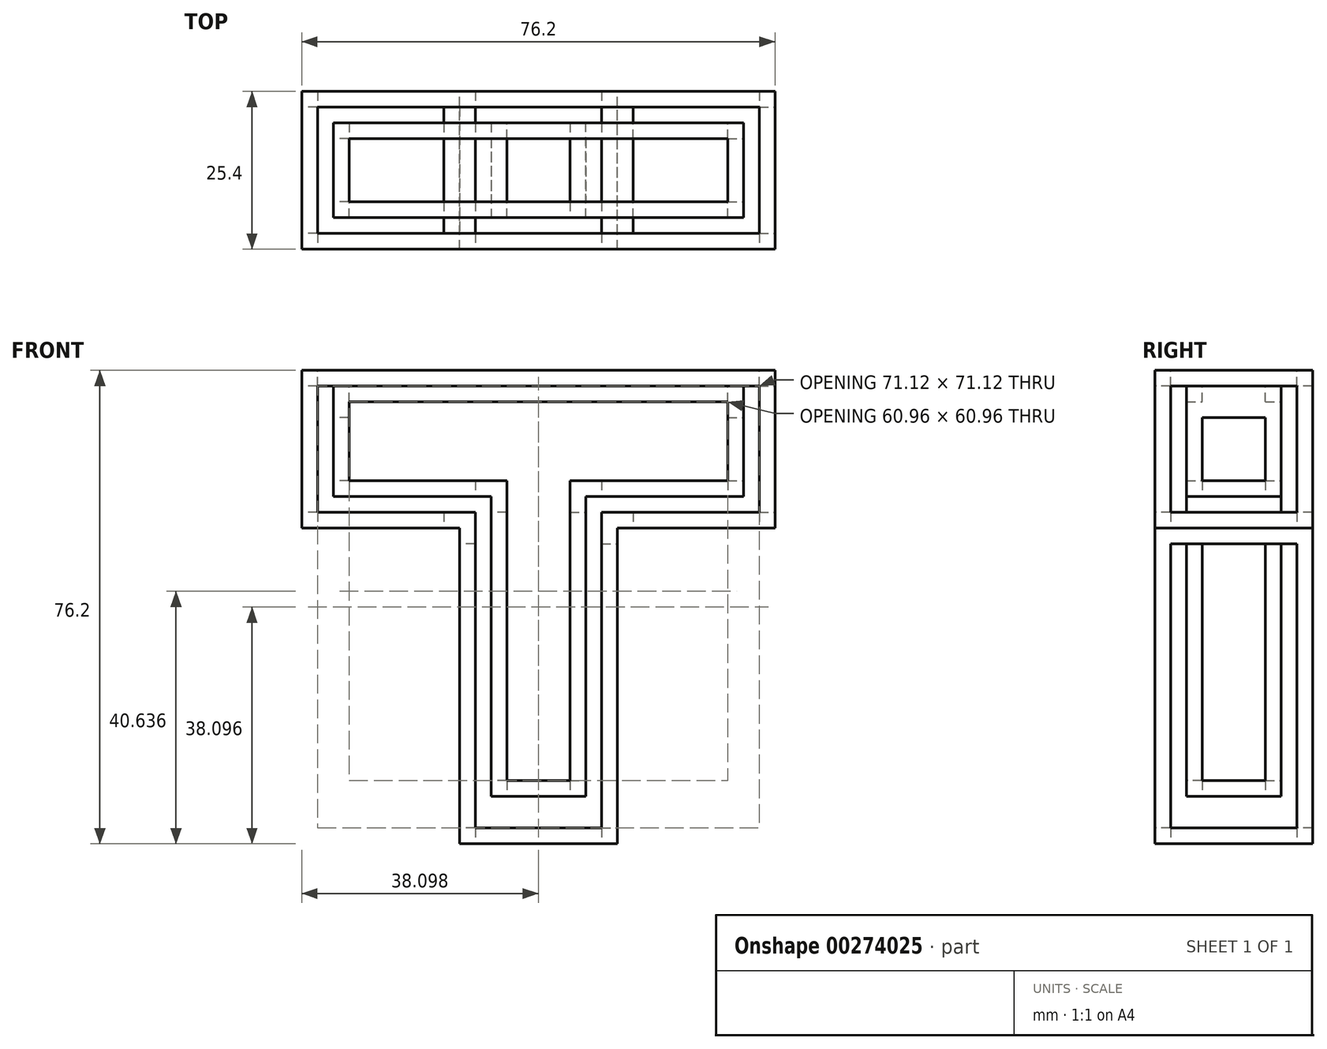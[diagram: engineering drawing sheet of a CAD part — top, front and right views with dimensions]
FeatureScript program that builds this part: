
annotation { "Feature Type Name" : "Feature", "Feature Type Description" : "" }
export const myFeature = defineFeature(function(context is Context, id is Id, definition is map)
    precondition{}
    {
        {
            var Q0;
            Q0=qCreatedBy(makeId("Front.planeOp"),FACE);
            var sketch = newSketch(context, id + "F0", { "sketchPlane" : qUnion([Q0])});
            skCircle(sketch, "E0.cCircle", {"center": v(-31.95, 20.43) * mm, "radius": 23.31 * mm, "construction": true});
            skLineSegment(sketch, "E0.0", {"start": v(-8.63, 33.9) * mm, "end": v(-8.63, 6.97) * mm});
            skLineSegment(sketch, "E0.1", {"start": v(-8.63, 6.97) * mm, "end": v(-31.95, -6.48) * mm});
            skLineSegment(sketch, "E0.2", {"start": v(-31.95, -6.48) * mm, "end": v(-55.26, 6.97) * mm});
            skLineSegment(sketch, "E0.3", {"start": v(-55.26, 6.97) * mm, "end": v(-55.26, 33.9) * mm});
            skLineSegment(sketch, "E0.4", {"start": v(-55.26, 33.9) * mm, "end": v(-31.95, 47.35) * mm});
            skLineSegment(sketch, "E0.5", {"start": v(-31.95, 47.35) * mm, "end": v(-8.63, 33.9) * mm});
            skPoint(sketch, "E0.0.midPoint", {"position": v(-8.63, 20.43) * mm});
            skSolve(sketch);
        }
        {
            var Q0;
            Q0 = qSketchRegion(id + "F0", true);
            extrude(context, id + "F1", {"entities" : qUnion([Q0]), "depth" : 25.4 * mm});
        }
        {
            var Q0;
            Q0=makeQuery(id+"F1.opExtrude","SWEPT_BODY",BODY,{"disambiguationData":[OSD([sQuery(id+"F0.wireOp",EDGE,"E0.0"),sQuery(id+"F0.wireOp",EDGE,"E0.1"),sQuery(id+"F0.wireOp",EDGE,"E0.2"),sQuery(id+"F0.wireOp",EDGE,"E0.3"),sQuery(id+"F0.wireOp",EDGE,"E0.4"),sQuery(id+"F0.wireOp",EDGE,"E0.5")])]});
            deleteBodies(context, id + "F2", {"entities" : qUnion([Q0])});
        }
        {
            var Q0;
            Q0=qCreatedBy(makeId("Front.planeOp"),FACE);
            var sketch = newSketch(context, id + "F3", { "sketchPlane" : qUnion([Q0])});
            skLineSegment(sketch, "E1", {"start": v(-61.41, 28.32) * mm, "end": v(14.79, 28.32) * mm});
            skLineSegment(sketch, "E2", {"start": v(14.79, 28.32) * mm, "end": v(14.79, 2.92) * mm});
            skLineSegment(sketch, "E3", {"start": v(14.79, 2.92) * mm, "end": v(-61.41, 2.92) * mm});
            skLineSegment(sketch, "E4", {"start": v(-61.41, 2.92) * mm, "end": v(-61.41, 28.32) * mm});
            skLineSegment(sketch, "E5", {"start": v(-23.31, 2.92) * mm, "end": v(-23.31, -47.88) * mm});
            skLineSegment(sketch, "E6", {"start": v(-23.31, -47.88) * mm, "end": v(-36.01, -47.88) * mm});
            skLineSegment(sketch, "E7", {"start": v(-36.01, -47.88) * mm, "end": v(-36.01, 2.92) * mm});
            skLineSegment(sketch, "E8", {"start": v(-23.31, -47.88) * mm, "end": v(-10.61, -47.88) * mm});
            skLineSegment(sketch, "E9", {"start": v(-10.61, -47.88) * mm, "end": v(-10.61, 2.92) * mm});
            skSolve(sketch);
        }
        {
            var Q0;
            Q0=makeQuery(id+"F3.imprint","IMPRINT",FACE,{"disambiguationData":[TD([[makeQuery(id+"F3.imprint","IMPRINT",EDGE,{"derivedFrom":sQuery(id+"F3.wireOp",EDGE,"E1")}),-1.0]])]});
            var Q1;
            {var subQ0=sQuery(id+"F3.wireOp",EDGE,"E5");Q1=makeQuery(id+"F3.imprint","IMPRINT",FACE,{"disambiguationData":[TD([[makeQuery(id+"F3.imprint","IMPRINT",EDGE,{"derivedFrom":subQ0}),-1.0]])]});}
            var Q2;
            {var subQ0=sQuery(id+"F3.wireOp",EDGE,"E5");Q2=makeQuery(id+"F3.imprint","IMPRINT",FACE,{"disambiguationData":[TD([[makeQuery(id+"F3.imprint","IMPRINT",EDGE,{"derivedFrom":subQ0}),1.0]])]});}
            extrude(context, id + "F4", {"entities" : qUnion([Q0, Q1, Q2]), "depth" : 12.7 * mm});
        }
        {
            var Q0;
            Q0=makeQuery(id+"F4.opExtrude","CAP_FACE",FACE,{"disambiguationData":[OSD([sQuery(id+"F3.wireOp",EDGE,"E1"),sQuery(id+"F3.wireOp",EDGE,"E2"),sQuery(id+"F3.wireOp",EDGE,"E3"),sQuery(id+"F3.wireOp",EDGE,"E4"),sQuery(id+"F3.wireOp",EDGE,"E6"),sQuery(id+"F3.wireOp",EDGE,"E7"),sQuery(id+"F3.wireOp",EDGE,"E8"),sQuery(id+"F3.wireOp",EDGE,"E9")])],"isStart":false});
            var sketch = newSketch(context, id + "F5", { "sketchPlane" : qUnion([Q0])});
            skLineSegment(sketch, "E10.0", {"start": v(-33.47, -45.34) * mm, "end": v(-13.15, -45.34) * mm});
            skLineSegment(sketch, "E10.1", {"start": v(-33.47, 5.46) * mm, "end": v(-33.47, -45.34) * mm});
            skLineSegment(sketch, "E10.2", {"start": v(-13.15, -45.34) * mm, "end": v(-13.15, 5.46) * mm});
            skLineSegment(sketch, "E10.3", {"start": v(-58.87, 5.46) * mm, "end": v(-33.47, 5.46) * mm});
            skLineSegment(sketch, "E10.4", {"start": v(-13.15, 5.46) * mm, "end": v(12.25, 5.46) * mm});
            skLineSegment(sketch, "E10.5", {"start": v(12.25, 5.46) * mm, "end": v(12.25, 25.78) * mm});
            skLineSegment(sketch, "E10.6", {"start": v(12.25, 25.78) * mm, "end": v(-58.87, 25.78) * mm});
            skLineSegment(sketch, "E10.7", {"start": v(-58.87, 25.78) * mm, "end": v(-58.87, 5.46) * mm});
            skSolve(sketch);
        }
        {
            var Q0;
            Q0=makeQuery(id+"F5.imprint","IMPRINT",FACE,{"disambiguationData":[TD([[makeQuery(id+"F5.imprint","IMPRINT",EDGE,{"derivedFrom":sQuery(id+"F5.wireOp",EDGE,"E10.0")}),1.0]])]});
            extrude(context, id + "F6", {"entities" : qUnion([Q0]), "operationType" : NewBodyOperationType.REMOVE, "oppositeDirection" : true, "depth" : 5.08 * mm});
        }
        {
            var Q0;
            Q0=makeQuery(id+"F4.opExtrude","SWEPT_BODY",BODY,{"disambiguationData":[OSD([sQuery(id+"F3.wireOp",EDGE,"E1"),sQuery(id+"F3.wireOp",EDGE,"E2"),sQuery(id+"F3.wireOp",EDGE,"E3"),sQuery(id+"F3.wireOp",EDGE,"E4"),sQuery(id+"F3.wireOp",EDGE,"E6"),sQuery(id+"F3.wireOp",EDGE,"E7"),sQuery(id+"F3.wireOp",EDGE,"E8"),sQuery(id+"F3.wireOp",EDGE,"E9")])]});
            var Q1;
            Q1=makeQuery(id+"F4.opExtrude","CAP_FACE",FACE,{"disambiguationData":[OSD([sQuery(id+"F3.wireOp",EDGE,"E1"),sQuery(id+"F3.wireOp",EDGE,"E2"),sQuery(id+"F3.wireOp",EDGE,"E3"),sQuery(id+"F3.wireOp",EDGE,"E4"),sQuery(id+"F3.wireOp",EDGE,"E6"),sQuery(id+"F3.wireOp",EDGE,"E7"),sQuery(id+"F3.wireOp",EDGE,"E8"),sQuery(id+"F3.wireOp",EDGE,"E9")])],"isStart":true});
            mirror(context, id + "F7", {"operationType" : NewBodyOperationType.ADD, "entities" : qUnion([Q0]), "mirrorPlane" : qUnion([Q1])});
        }
        {
            var Q0;
            Q0=makeQuery(id+"F7.opPattern","COPY",FACE,{"derivedFrom":makeQuery(id+"F6.boolean.opBoolean","COPY",FACE,{"derivedFrom":makeQuery(id+"F6.opExtrude","CAP_FACE",FACE,{"disambiguationData":[OSD([sQuery(id+"F5.wireOp",EDGE,"E10.0"),sQuery(id+"F5.wireOp",EDGE,"E10.1"),sQuery(id+"F5.wireOp",EDGE,"E10.2"),sQuery(id+"F5.wireOp",EDGE,"E10.3"),sQuery(id+"F5.wireOp",EDGE,"E10.4"),sQuery(id+"F5.wireOp",EDGE,"E10.5"),sQuery(id+"F5.wireOp",EDGE,"E10.6"),sQuery(id+"F5.wireOp",EDGE,"E10.7")])],"isStart":false})}),"instanceName":"1"});
            var sketch = newSketch(context, id + "F8", { "sketchPlane" : qUnion([Q0])});
            skLineSegment(sketch, "E11.0", {"start": v(56.33, 8) * mm, "end": v(56.33, 23.24) * mm});
            skLineSegment(sketch, "E11.1", {"start": v(30.93, 8) * mm, "end": v(56.33, 8) * mm});
            skLineSegment(sketch, "E11.2", {"start": v(56.33, 23.24) * mm, "end": v(-9.7, 23.24) * mm});
            skLineSegment(sketch, "E11.3", {"start": v(30.93, -42.8) * mm, "end": v(30.93, 8) * mm});
            skLineSegment(sketch, "E11.4", {"start": v(-9.7, 23.24) * mm, "end": v(-9.7, 8) * mm});
            skLineSegment(sketch, "E11.5", {"start": v(-9.7, 8) * mm, "end": v(15.7, 8) * mm});
            skLineSegment(sketch, "E11.6", {"start": v(15.7, 8) * mm, "end": v(15.7, -42.8) * mm});
            skLineSegment(sketch, "E11.7", {"start": v(15.7, -42.8) * mm, "end": v(30.93, -42.8) * mm});
            skSolve(sketch);
        }
        {
            var Q0;
            Q0=makeQuery(id+"F8.imprint","IMPRINT",FACE,{"disambiguationData":[TD([[makeQuery(id+"F8.imprint","IMPRINT",EDGE,{"derivedFrom":sQuery(id+"F8.wireOp",EDGE,"E11.0")}),-1.0]])]});
            extrude(context, id + "F9", {"entities" : qUnion([Q0]), "operationType" : NewBodyOperationType.REMOVE, "oppositeDirection" : true, "depth" : 25.4 * mm});
        }
        {
            var Q0;
            Q0=makeQuery(id+"F7.opPattern","COPY",FACE,{"derivedFrom":makeQuery(id+"F6.boolean.opBoolean","COPY",FACE,{"derivedFrom":makeQuery(id+"F6.opExtrude","CAP_FACE",FACE,{"disambiguationData":[OSD([sQuery(id+"F5.wireOp",EDGE,"E10.0"),sQuery(id+"F5.wireOp",EDGE,"E10.1"),sQuery(id+"F5.wireOp",EDGE,"E10.2"),sQuery(id+"F5.wireOp",EDGE,"E10.3"),sQuery(id+"F5.wireOp",EDGE,"E10.4"),sQuery(id+"F5.wireOp",EDGE,"E10.5"),sQuery(id+"F5.wireOp",EDGE,"E10.6"),sQuery(id+"F5.wireOp",EDGE,"E10.7")])],"isStart":false})}),"instanceName":"1"});
            var sketch = newSketch(context, id + "F10", { "sketchPlane" : qUnion([Q0])});
            skLineSegment(sketch, "E12.0", {"start": v(-7.17, 10.54) * mm, "end": v(18.23, 10.54) * mm});
            skLineSegment(sketch, "E12.1", {"start": v(-7.17, 20.7) * mm, "end": v(-7.17, 10.54) * mm});
            skLineSegment(sketch, "E12.2", {"start": v(18.23, 10.54) * mm, "end": v(18.23, -40.26) * mm});
            skLineSegment(sketch, "E12.3", {"start": v(53.8, 20.7) * mm, "end": v(-7.17, 20.7) * mm});
            skLineSegment(sketch, "E12.4", {"start": v(18.23, -40.26) * mm, "end": v(28.4, -40.26) * mm});
            skLineSegment(sketch, "E12.5", {"start": v(28.4, -40.26) * mm, "end": v(28.4, 10.54) * mm});
            skLineSegment(sketch, "E12.6", {"start": v(28.4, 10.54) * mm, "end": v(53.8, 10.54) * mm});
            skLineSegment(sketch, "E12.7", {"start": v(53.8, 10.54) * mm, "end": v(53.8, 20.7) * mm});
            skSolve(sketch);
        }
        {
            var Q0;
            Q0=makeQuery(id+"F10.imprint","IMPRINT",FACE,{"disambiguationData":[TD([[makeQuery(id+"F10.imprint","IMPRINT",EDGE,{"derivedFrom":sQuery(id+"F10.wireOp",EDGE,"E12.0")}),1.0]])]});
            extrude(context, id + "F11", {"entities" : qUnion([Q0]), "operationType" : NewBodyOperationType.REMOVE, "oppositeDirection" : true, "depth" : 25.4 * mm});
        }
        {
            var Q0;
            {var subQ0=makeQuery(id+"F4.opExtrude","SWEPT_FACE",FACE,{"disambiguationData":[OSD([sQuery(id+"F3.wireOp",EDGE,"E9")])]});Q0=makeQuery(id+"F7.boolean.opBoolean","MERGE",FACE,{"derivedFrom":[subQ0,makeQuery(id+"F7.opPattern","COPY",FACE,{"derivedFrom":subQ0,"instanceName":"1"})]});}
            var sketch = newSketch(context, id + "F12", { "sketchPlane" : qUnion([Q0])});
            skLineSegment(sketch, "E13.0", {"start": v(-10.16, -45.34) * mm, "end": v(10.16, -45.34) * mm});
            skLineSegment(sketch, "E13.1", {"start": v(-10.16, 0.38) * mm, "end": v(-10.16, -45.34) * mm});
            skLineSegment(sketch, "E13.2", {"start": v(10.16, 0.38) * mm, "end": v(-10.16, 0.38) * mm});
            skLineSegment(sketch, "E13.3", {"start": v(10.16, -45.34) * mm, "end": v(10.16, 0.38) * mm});
            skSolve(sketch);
        }
        {
            var Q0;
            Q0=makeQuery(id+"F12.imprint","IMPRINT",FACE,{"disambiguationData":[TD([[makeQuery(id+"F12.imprint","IMPRINT",EDGE,{"derivedFrom":sQuery(id+"F12.wireOp",EDGE,"E13.0")}),1.0]])]});
            extrude(context, id + "F13", {"entities" : qUnion([Q0]), "operationType" : NewBodyOperationType.REMOVE, "oppositeDirection" : true, "depth" : 2.54 * mm});
        }
        {
            var Q0;
            {var subQ0=makeQuery(id+"F4.opExtrude","SWEPT_FACE",FACE,{"disambiguationData":[OSD([sQuery(id+"F3.wireOp",EDGE,"E7")])]});Q0=makeQuery(id+"F7.boolean.opBoolean","MERGE",FACE,{"derivedFrom":[subQ0,makeQuery(id+"F7.opPattern","COPY",FACE,{"derivedFrom":subQ0,"instanceName":"1"})]});}
            var sketch = newSketch(context, id + "F14", { "sketchPlane" : qUnion([Q0])});
            skLineSegment(sketch, "E14.0", {"start": v(10.16, 0.38) * mm, "end": v(-10.16, 0.38) * mm});
            skLineSegment(sketch, "E14.1", {"start": v(10.16, -45.34) * mm, "end": v(10.16, 0.38) * mm});
            skLineSegment(sketch, "E14.2", {"start": v(-10.16, -45.34) * mm, "end": v(10.16, -45.34) * mm});
            skLineSegment(sketch, "E14.3", {"start": v(-10.16, 0.38) * mm, "end": v(-10.16, -45.34) * mm});
            skSolve(sketch);
        }
        {
            var Q0;
            Q0=makeQuery(id+"F14.imprint","IMPRINT",FACE,{"disambiguationData":[TD([[makeQuery(id+"F14.imprint","IMPRINT",EDGE,{"derivedFrom":sQuery(id+"F14.wireOp",EDGE,"E14.0")}),1.0]])]});
            extrude(context, id + "F15", {"entities" : qUnion([Q0]), "operationType" : NewBodyOperationType.REMOVE, "oppositeDirection" : true, "depth" : 2.54 * mm});
        }
        {
            var Q0;
            {var subQ0=makeQuery(id+"F4.opExtrude","SWEPT_FACE",FACE,{"disambiguationData":[OSD([sQuery(id+"F3.wireOp",EDGE,"E2")])]});Q0=makeQuery(id+"F7.boolean.opBoolean","MERGE",FACE,{"derivedFrom":[subQ0,makeQuery(id+"F7.opPattern","COPY",FACE,{"derivedFrom":subQ0,"instanceName":"1"})]});}
            var sketch = newSketch(context, id + "F16", { "sketchPlane" : qUnion([Q0])});
            skLineSegment(sketch, "E15.0", {"start": v(-10.16, 5.46) * mm, "end": v(10.16, 5.46) * mm});
            skLineSegment(sketch, "E15.1", {"start": v(-10.16, 25.78) * mm, "end": v(-10.16, 5.46) * mm});
            skLineSegment(sketch, "E15.2", {"start": v(10.16, 25.78) * mm, "end": v(-10.16, 25.78) * mm});
            skLineSegment(sketch, "E15.3", {"start": v(10.16, 5.46) * mm, "end": v(10.16, 25.78) * mm});
            skSolve(sketch);
        }
        {
            var Q0;
            Q0=makeQuery(id+"F16.imprint","IMPRINT",FACE,{"disambiguationData":[TD([[makeQuery(id+"F16.imprint","IMPRINT",EDGE,{"derivedFrom":sQuery(id+"F16.wireOp",EDGE,"E15.0")}),1.0]])]});
            extrude(context, id + "F17", {"entities" : qUnion([Q0]), "operationType" : NewBodyOperationType.REMOVE, "oppositeDirection" : true, "depth" : 2.54 * mm});
        }
        {
            var Q0;
            {var subQ0=makeQuery(id+"F4.opExtrude","SWEPT_FACE",FACE,{"disambiguationData":[OSD([sQuery(id+"F3.wireOp",EDGE,"E4")])]});Q0=makeQuery(id+"F7.boolean.opBoolean","MERGE",FACE,{"derivedFrom":[subQ0,makeQuery(id+"F7.opPattern","COPY",FACE,{"derivedFrom":subQ0,"instanceName":"1"})]});}
            var sketch = newSketch(context, id + "F18", { "sketchPlane" : qUnion([Q0])});
            skLineSegment(sketch, "E16.0", {"start": v(10.16, 25.78) * mm, "end": v(-10.16, 25.78) * mm});
            skLineSegment(sketch, "E16.1", {"start": v(10.16, 5.46) * mm, "end": v(10.16, 25.78) * mm});
            skLineSegment(sketch, "E16.2", {"start": v(-10.16, 5.46) * mm, "end": v(10.16, 5.46) * mm});
            skLineSegment(sketch, "E16.3", {"start": v(-10.16, 25.78) * mm, "end": v(-10.16, 5.46) * mm});
            skSolve(sketch);
        }
        {
            var Q0;
            Q0=makeQuery(id+"F18.imprint","IMPRINT",FACE,{"disambiguationData":[TD([[makeQuery(id+"F18.imprint","IMPRINT",EDGE,{"derivedFrom":sQuery(id+"F18.wireOp",EDGE,"E16.0")}),1.0]])]});
            extrude(context, id + "F19", {"entities" : qUnion([Q0]), "operationType" : NewBodyOperationType.REMOVE, "oppositeDirection" : true, "depth" : 2.54 * mm});
        }
        {
            var Q0;
            {var subQ0=makeQuery(id+"F4.opExtrude","SWEPT_FACE",FACE,{"disambiguationData":[OSD([sQuery(id+"F3.wireOp",EDGE,"E6"),sQuery(id+"F3.wireOp",EDGE,"E8")])]});Q0=makeQuery(id+"F7.boolean.opBoolean","MERGE",FACE,{"derivedFrom":[subQ0,makeQuery(id+"F7.opPattern","COPY",FACE,{"derivedFrom":subQ0,"instanceName":"1"})]});}
            var sketch = newSketch(context, id + "F20", { "sketchPlane" : qUnion([Q0])});
            skLineSegment(sketch, "E17.0", {"start": v(-33.47, 10.16) * mm, "end": v(-33.47, -10.16) * mm});
            skLineSegment(sketch, "E17.1", {"start": v(-13.15, 10.16) * mm, "end": v(-33.47, 10.16) * mm});
            skLineSegment(sketch, "E17.2", {"start": v(-13.15, -10.16) * mm, "end": v(-13.15, 10.16) * mm});
            skLineSegment(sketch, "E17.3", {"start": v(-33.47, -10.16) * mm, "end": v(-13.15, -10.16) * mm});
            skSolve(sketch);
        }
        {
            var Q0;
            Q0=makeQuery(id+"F20.imprint","IMPRINT",FACE,{"disambiguationData":[TD([[makeQuery(id+"F20.imprint","IMPRINT",EDGE,{"derivedFrom":sQuery(id+"F20.wireOp",EDGE,"E17.0")}),1.0]])]});
            extrude(context, id + "F21", {"entities" : qUnion([Q0]), "operationType" : NewBodyOperationType.REMOVE, "oppositeDirection" : true, "depth" : 2.54 * mm});
        }
        {
            var Q0;
            {var subQ0=makeQuery(id+"F4.opExtrude","SWEPT_FACE",FACE,{"disambiguationData":[OSD([sQuery(id+"F3.wireOp",EDGE,"E1")])]});Q0=makeQuery(id+"F7.boolean.opBoolean","MERGE",FACE,{"derivedFrom":[subQ0,makeQuery(id+"F7.opPattern","COPY",FACE,{"derivedFrom":subQ0,"instanceName":"1"})]});}
            var sketch = newSketch(context, id + "F22", { "sketchPlane" : qUnion([Q0])});
            skLineSegment(sketch, "E18.0", {"start": v(12.25, -10.16) * mm, "end": v(12.25, 10.16) * mm});
            skLineSegment(sketch, "E18.1", {"start": v(-58.87, -10.16) * mm, "end": v(12.25, -10.16) * mm});
            skLineSegment(sketch, "E18.2", {"start": v(-58.87, 10.16) * mm, "end": v(-58.87, -10.16) * mm});
            skLineSegment(sketch, "E18.3", {"start": v(12.25, 10.16) * mm, "end": v(-58.87, 10.16) * mm});
            skSolve(sketch);
        }
        {
            var Q0;
            Q0=makeQuery(id+"F22.imprint","IMPRINT",FACE,{"disambiguationData":[TD([[makeQuery(id+"F22.imprint","IMPRINT",EDGE,{"derivedFrom":sQuery(id+"F22.wireOp",EDGE,"E18.0")}),1.0]])]});
            extrude(context, id + "F23", {"entities" : qUnion([Q0]), "operationType" : NewBodyOperationType.REMOVE, "oppositeDirection" : true, "depth" : 2.54 * mm});
        }
        {
            var Q0;
            {var subQ0=sQuery(id+"F3.wireOp",EDGE,"E3");var subQ1=makeQuery(id+"F4.opExtrude","SWEPT_FACE",FACE,{"disambiguationData":[OSD([subQ0]),TDD([makeQuery(id+"F3.imprint","IMPRINT",EDGE,{"disambiguationData":[TD([[makeQuery(id+"F3.imprint","INTERSECT",VERTEX,{"derivedFrom":[sQuery(id+"F3.wireOp",EDGE,"E2"),subQ0]}),-1.0]])],"derivedFrom":subQ0})])]});Q0=makeQuery(id+"F7.boolean.opBoolean","MERGE",FACE,{"derivedFrom":[subQ1,makeQuery(id+"F7.opPattern","COPY",FACE,{"derivedFrom":subQ1,"instanceName":"1"})]});}
            var sketch = newSketch(context, id + "F24", { "sketchPlane" : qUnion([Q0])});
            skLineSegment(sketch, "E19.0", {"start": v(-8.07, 10.16) * mm, "end": v(-8.07, -10.16) * mm});
            skLineSegment(sketch, "E19.1", {"start": v(12.25, 10.16) * mm, "end": v(-8.07, 10.16) * mm});
            skLineSegment(sketch, "E19.2", {"start": v(12.25, -10.16) * mm, "end": v(12.25, 10.16) * mm});
            skLineSegment(sketch, "E19.3", {"start": v(-8.07, -10.16) * mm, "end": v(12.25, -10.16) * mm});
            skSolve(sketch);
        }
        {
            var Q0;
            {var subQ0=sQuery(id+"F3.wireOp",EDGE,"E3");var subQ1=makeQuery(id+"F4.opExtrude","SWEPT_FACE",FACE,{"disambiguationData":[OSD([subQ0]),TDD([makeQuery(id+"F3.imprint","IMPRINT",EDGE,{"disambiguationData":[TD([[makeQuery(id+"F3.imprint","INTERSECT",VERTEX,{"derivedFrom":[subQ0,sQuery(id+"F3.wireOp",EDGE,"E4")]}),1.0]])],"derivedFrom":subQ0})])]});Q0=makeQuery(id+"F7.boolean.opBoolean","MERGE",FACE,{"derivedFrom":[subQ1,makeQuery(id+"F7.opPattern","COPY",FACE,{"derivedFrom":subQ1,"instanceName":"1"})]});}
            var sketch = newSketch(context, id + "F25", { "sketchPlane" : qUnion([Q0])});
            skLineSegment(sketch, "E20.0", {"start": v(-58.87, 10.16) * mm, "end": v(-58.87, -10.16) * mm});
            skLineSegment(sketch, "E20.1", {"start": v(-38.55, 10.16) * mm, "end": v(-58.87, 10.16) * mm});
            skLineSegment(sketch, "E20.2", {"start": v(-38.55, -10.16) * mm, "end": v(-38.55, 10.16) * mm});
            skLineSegment(sketch, "E20.3", {"start": v(-58.87, -10.16) * mm, "end": v(-38.55, -10.16) * mm});
            skSolve(sketch);
        }
        {
            var Q0;
            Q0=makeQuery(id+"F25.imprint","IMPRINT",FACE,{"disambiguationData":[TD([[makeQuery(id+"F25.imprint","IMPRINT",EDGE,{"derivedFrom":sQuery(id+"F25.wireOp",EDGE,"E20.0")}),1.0]])]});
            var Q1;
            Q1=makeQuery(id+"F24.imprint","IMPRINT",FACE,{"disambiguationData":[TD([[makeQuery(id+"F24.imprint","IMPRINT",EDGE,{"derivedFrom":sQuery(id+"F24.wireOp",EDGE,"E19.0")}),1.0]])]});
            extrude(context, id + "F26", {"entities" : qUnion([Q0, Q1]), "operationType" : NewBodyOperationType.REMOVE, "oppositeDirection" : true, "depth" : 2.54 * mm});
        }
        {
            var Q0;
            Q0=makeQuery(id+"F9.boolean.opBoolean","COPY",FACE,{"derivedFrom":makeQuery(id+"F9.opExtrude","SWEPT_FACE",FACE,{"disambiguationData":[OSD([sQuery(id+"F8.wireOp",EDGE,"E11.3")])]})});
            var sketch = newSketch(context, id + "F27", { "sketchPlane" : qUnion([Q0])});
            skLineSegment(sketch, "E21.0", {"start": v(5.08, 5.46) * mm, "end": v(-5.08, 5.46) * mm});
            skLineSegment(sketch, "E21.1", {"start": v(5.08, -40.26) * mm, "end": v(5.08, 5.46) * mm});
            skLineSegment(sketch, "E21.2", {"start": v(-5.08, -40.26) * mm, "end": v(5.08, -40.26) * mm});
            skLineSegment(sketch, "E21.3", {"start": v(-5.08, 5.46) * mm, "end": v(-5.08, -40.26) * mm});
            skSolve(sketch);
        }
        {
            var Q0;
            Q0=makeQuery(id+"F27.imprint","IMPRINT",FACE,{"disambiguationData":[TD([[makeQuery(id+"F27.imprint","IMPRINT",EDGE,{"derivedFrom":sQuery(id+"F27.wireOp",EDGE,"E21.0")}),1.0]])]});
            extrude(context, id + "F28", {"entities" : qUnion([Q0]), "operationType" : NewBodyOperationType.REMOVE, "oppositeDirection" : true, "depth" : 2.54 * mm});
        }
        {
            var Q0;
            Q0=makeQuery(id+"F9.boolean.opBoolean","COPY",FACE,{"derivedFrom":makeQuery(id+"F9.opExtrude","SWEPT_FACE",FACE,{"disambiguationData":[OSD([sQuery(id+"F8.wireOp",EDGE,"E11.6")])]})});
            var sketch = newSketch(context, id + "F29", { "sketchPlane" : qUnion([Q0])});
            skLineSegment(sketch, "E22.0", {"start": v(-5.08, -40.26) * mm, "end": v(5.08, -40.26) * mm});
            skLineSegment(sketch, "E22.1", {"start": v(-5.08, 5.46) * mm, "end": v(-5.08, -40.26) * mm});
            skLineSegment(sketch, "E22.2", {"start": v(5.08, 5.46) * mm, "end": v(-5.08, 5.46) * mm});
            skLineSegment(sketch, "E22.3", {"start": v(5.08, -40.26) * mm, "end": v(5.08, 5.46) * mm});
            skSolve(sketch);
        }
        {
            var Q0;
            Q0=makeQuery(id+"F29.imprint","IMPRINT",FACE,{"disambiguationData":[TD([[makeQuery(id+"F29.imprint","IMPRINT",EDGE,{"derivedFrom":sQuery(id+"F29.wireOp",EDGE,"E22.0")}),1.0]])]});
            extrude(context, id + "F30", {"entities" : qUnion([Q0]), "operationType" : NewBodyOperationType.REMOVE, "oppositeDirection" : true, "depth" : 2.54 * mm});
        }
        {
            var Q0;
            Q0=makeQuery(id+"F9.boolean.opBoolean","COPY",FACE,{"derivedFrom":makeQuery(id+"F9.opExtrude","SWEPT_FACE",FACE,{"disambiguationData":[OSD([sQuery(id+"F8.wireOp",EDGE,"E11.5")])]})});
            var sketch = newSketch(context, id + "F31", { "sketchPlane" : qUnion([Q0])});
            skLineSegment(sketch, "E23.0", {"start": v(-13.15, 5.08) * mm, "end": v(-13.15, -5.08) * mm});
            skLineSegment(sketch, "E23.1", {"start": v(7.17, 5.08) * mm, "end": v(-13.15, 5.08) * mm});
            skLineSegment(sketch, "E23.2", {"start": v(7.17, -5.08) * mm, "end": v(7.17, 5.08) * mm});
            skLineSegment(sketch, "E23.3", {"start": v(-13.15, -5.08) * mm, "end": v(7.17, -5.08) * mm});
            skSolve(sketch);
        }
        {
            var Q0;
            Q0=makeQuery(id+"F31.imprint","IMPRINT",FACE,{"disambiguationData":[TD([[makeQuery(id+"F31.imprint","IMPRINT",EDGE,{"derivedFrom":sQuery(id+"F31.wireOp",EDGE,"E23.0")}),1.0]])]});
            extrude(context, id + "F32", {"entities" : qUnion([Q0]), "operationType" : NewBodyOperationType.REMOVE, "oppositeDirection" : true, "depth" : 2.54 * mm});
        }
        {
            var Q0;
            Q0=makeQuery(id+"F9.boolean.opBoolean","COPY",FACE,{"derivedFrom":makeQuery(id+"F9.opExtrude","SWEPT_FACE",FACE,{"disambiguationData":[OSD([sQuery(id+"F8.wireOp",EDGE,"E11.1")])]})});
            var sketch = newSketch(context, id + "F33", { "sketchPlane" : qUnion([Q0])});
            skLineSegment(sketch, "E24.0", {"start": v(-53.8, 5.08) * mm, "end": v(-53.8, -5.08) * mm});
            skLineSegment(sketch, "E24.1", {"start": v(-33.47, 5.08) * mm, "end": v(-53.8, 5.08) * mm});
            skLineSegment(sketch, "E24.2", {"start": v(-33.47, -5.08) * mm, "end": v(-33.47, 5.08) * mm});
            skLineSegment(sketch, "E24.3", {"start": v(-53.8, -5.08) * mm, "end": v(-33.47, -5.08) * mm});
            skSolve(sketch);
        }
        {
            var Q0;
            Q0=makeQuery(id+"F33.imprint","IMPRINT",FACE,{"disambiguationData":[TD([[makeQuery(id+"F33.imprint","IMPRINT",EDGE,{"derivedFrom":sQuery(id+"F33.wireOp",EDGE,"E24.0")}),1.0]])]});
            extrude(context, id + "F34", {"entities" : qUnion([Q0]), "operationType" : NewBodyOperationType.REMOVE, "oppositeDirection" : true, "depth" : 2.54 * mm});
        }
        {
            var Q0;
            Q0=makeQuery(id+"F9.boolean.opBoolean","COPY",FACE,{"derivedFrom":makeQuery(id+"F9.opExtrude","SWEPT_FACE",FACE,{"disambiguationData":[OSD([sQuery(id+"F8.wireOp",EDGE,"E11.4")])]})});
            var sketch = newSketch(context, id + "F35", { "sketchPlane" : qUnion([Q0])});
            skLineSegment(sketch, "E25.0", {"start": v(-5.08, 10.54) * mm, "end": v(5.08, 10.54) * mm});
            skLineSegment(sketch, "E25.1", {"start": v(-5.08, 20.7) * mm, "end": v(-5.08, 10.54) * mm});
            skLineSegment(sketch, "E25.2", {"start": v(5.08, 20.7) * mm, "end": v(-5.08, 20.7) * mm});
            skLineSegment(sketch, "E25.3", {"start": v(5.08, 10.54) * mm, "end": v(5.08, 20.7) * mm});
            skSolve(sketch);
        }
        {
            var Q0;
            Q0=makeQuery(id+"F35.imprint","IMPRINT",FACE,{"disambiguationData":[TD([[makeQuery(id+"F35.imprint","IMPRINT",EDGE,{"derivedFrom":sQuery(id+"F35.wireOp",EDGE,"E25.0")}),1.0]])]});
            extrude(context, id + "F36", {"entities" : qUnion([Q0]), "operationType" : NewBodyOperationType.REMOVE, "oppositeDirection" : true, "depth" : 2.54 * mm});
        }
        {
            var Q0;
            Q0=makeQuery(id+"F9.boolean.opBoolean","COPY",FACE,{"derivedFrom":makeQuery(id+"F9.opExtrude","SWEPT_FACE",FACE,{"disambiguationData":[OSD([sQuery(id+"F8.wireOp",EDGE,"E11.0")])]})});
            var sketch = newSketch(context, id + "F37", { "sketchPlane" : qUnion([Q0])});
            skLineSegment(sketch, "E26.0", {"start": v(5.08, 20.7) * mm, "end": v(-5.08, 20.7) * mm});
            skLineSegment(sketch, "E26.1", {"start": v(5.08, 10.54) * mm, "end": v(5.08, 20.7) * mm});
            skLineSegment(sketch, "E26.2", {"start": v(-5.08, 10.54) * mm, "end": v(5.08, 10.54) * mm});
            skLineSegment(sketch, "E26.3", {"start": v(-5.08, 20.7) * mm, "end": v(-5.08, 10.54) * mm});
            skSolve(sketch);
        }
        {
            var Q0;
            Q0=makeQuery(id+"F37.imprint","IMPRINT",FACE,{"disambiguationData":[TD([[makeQuery(id+"F37.imprint","IMPRINT",EDGE,{"derivedFrom":sQuery(id+"F37.wireOp",EDGE,"E26.0")}),1.0]])]});
            extrude(context, id + "F38", {"entities" : qUnion([Q0]), "operationType" : NewBodyOperationType.REMOVE, "oppositeDirection" : true, "depth" : 2.54 * mm});
        }
        {
            var Q0;
            Q0=makeQuery(id+"F9.boolean.opBoolean","COPY",FACE,{"derivedFrom":makeQuery(id+"F9.opExtrude","SWEPT_FACE",FACE,{"disambiguationData":[OSD([sQuery(id+"F8.wireOp",EDGE,"E11.7")])]})});
            var sketch = newSketch(context, id + "F39", { "sketchPlane" : qUnion([Q0])});
            skLineSegment(sketch, "E27.0", {"start": v(-28.4, 5.08) * mm, "end": v(-28.4, -5.08) * mm});
            skLineSegment(sketch, "E27.1", {"start": v(-18.23, 5.08) * mm, "end": v(-28.4, 5.08) * mm});
            skLineSegment(sketch, "E27.2", {"start": v(-18.23, -5.08) * mm, "end": v(-18.23, 5.08) * mm});
            skLineSegment(sketch, "E27.3", {"start": v(-28.4, -5.08) * mm, "end": v(-18.23, -5.08) * mm});
            skSolve(sketch);
        }
        {
            var Q0;
            Q0=makeQuery(id+"F39.imprint","IMPRINT",FACE,{"disambiguationData":[TD([[makeQuery(id+"F39.imprint","IMPRINT",EDGE,{"derivedFrom":sQuery(id+"F39.wireOp",EDGE,"E27.0")}),1.0]])]});
            extrude(context, id + "F40", {"entities" : qUnion([Q0]), "operationType" : NewBodyOperationType.REMOVE, "oppositeDirection" : true, "depth" : 2.54 * mm});
        }
        {
            var Q0;
            Q0=makeQuery(id+"F9.boolean.opBoolean","COPY",FACE,{"derivedFrom":makeQuery(id+"F9.opExtrude","SWEPT_FACE",FACE,{"disambiguationData":[OSD([sQuery(id+"F8.wireOp",EDGE,"E11.2")])]})});
            var sketch = newSketch(context, id + "F41", { "sketchPlane" : qUnion([Q0])});
            skLineSegment(sketch, "E28.0", {"start": v(7.17, -5.08) * mm, "end": v(7.17, 5.08) * mm});
            skLineSegment(sketch, "E28.1", {"start": v(-53.8, -5.08) * mm, "end": v(7.17, -5.08) * mm});
            skLineSegment(sketch, "E28.2", {"start": v(-53.8, 5.08) * mm, "end": v(-53.8, -5.08) * mm});
            skLineSegment(sketch, "E28.3", {"start": v(7.17, 5.08) * mm, "end": v(-53.8, 5.08) * mm});
            skSolve(sketch);
        }
        {
            var Q0;
            Q0=makeQuery(id+"F41.imprint","IMPRINT",FACE,{"disambiguationData":[TD([[makeQuery(id+"F41.imprint","IMPRINT",EDGE,{"derivedFrom":sQuery(id+"F41.wireOp",EDGE,"E28.0")}),1.0]])]});
            extrude(context, id + "F42", {"entities" : qUnion([Q0]), "operationType" : NewBodyOperationType.REMOVE, "oppositeDirection" : true, "depth" : 2.54 * mm});
        }
        {
            var Q0;
            Q0=makeQuery(id+"F6.boolean.opBoolean","COPY",FACE,{"derivedFrom":makeQuery(id+"F6.opExtrude","CAP_FACE",FACE,{"disambiguationData":[OSD([sQuery(id+"F5.wireOp",EDGE,"E10.0"),sQuery(id+"F5.wireOp",EDGE,"E10.1"),sQuery(id+"F5.wireOp",EDGE,"E10.2"),sQuery(id+"F5.wireOp",EDGE,"E10.3"),sQuery(id+"F5.wireOp",EDGE,"E10.4"),sQuery(id+"F5.wireOp",EDGE,"E10.5"),sQuery(id+"F5.wireOp",EDGE,"E10.6"),sQuery(id+"F5.wireOp",EDGE,"E10.7")])],"isStart":false})});
            var sketch = newSketch(context, id + "F43", { "sketchPlane" : qUnion([Q0])});
            skLineSegment(sketch, "E29", {"start": v(-28.4, -40.26) * mm, "end": v(-30.93, -40.26) * mm});
            skLineSegment(sketch, "E30", {"start": v(-18.23, -40.26) * mm, "end": v(-15.7, -40.26) * mm});
            skLineSegment(sketch, "E31", {"start": v(-15.7, -40.26) * mm, "end": v(-15.7, -37.72) * mm});
            skLineSegment(sketch, "E32", {"start": v(-15.7, -37.72) * mm, "end": v(-30.93, -37.72) * mm});
            skSolve(sketch);
        }
        {
            var Q0;
            {var subQ0=sQuery(id+"F43.wireOp",EDGE,"E29");Q0=makeQuery(id+"F43.imprint","IMPRINT",FACE,{"disambiguationData":[TD([[makeQuery(id+"F43.imprint","IMPRINT",EDGE,{"derivedFrom":subQ0}),-1.0]])]});}
            var Q1;
            {var subQ1=makeQuery(id+"F6.boolean.opBoolean","COPY",FACE,{"derivedFrom":makeQuery(id+"F6.opExtrude","CAP_FACE",FACE,{"disambiguationData":[OSD([sQuery(id+"F5.wireOp",EDGE,"E10.0"),sQuery(id+"F5.wireOp",EDGE,"E10.1"),sQuery(id+"F5.wireOp",EDGE,"E10.2"),sQuery(id+"F5.wireOp",EDGE,"E10.3"),sQuery(id+"F5.wireOp",EDGE,"E10.4"),sQuery(id+"F5.wireOp",EDGE,"E10.5"),sQuery(id+"F5.wireOp",EDGE,"E10.6"),sQuery(id+"F5.wireOp",EDGE,"E10.7")])],"isStart":false})});var subQ6=makeQuery(id+"F11.boolean.opBoolean","INTERSECT",EDGE,{"derivedFrom":[subQ1,makeQuery(id+"F11.opExtrude","SWEPT_FACE",FACE,{"disambiguationData":[OSD([sQuery(id+"F10.wireOp",EDGE,"E12.4")])]})]});Q1=makeQuery(id+"F43.imprint","IMPRINT",FACE,{"disambiguationData":[TD([[makeQuery(id+"F43.imprint","IMPRINT",EDGE,{"derivedFrom":subQ6}),1.0]])]});}
            var Q2;
            {var subQ0=sQuery(id+"F43.wireOp",EDGE,"E30");Q2=makeQuery(id+"F43.imprint","IMPRINT",FACE,{"disambiguationData":[TD([[makeQuery(id+"F43.imprint","IMPRINT",EDGE,{"derivedFrom":subQ0}),1.0]])]});}
            extrude(context, id + "F44", {"entities" : qUnion([Q0, Q1, Q2]), "operationType" : NewBodyOperationType.ADD, "oppositeDirection" : true, "depth" : 15.24 * mm});
        }
        {
            var Q0;
            {var subQ0=sQuery(id+"F8.wireOp",EDGE,"E11.3");Q0=makeQuery(id+"F44.boolean.opBoolean","MERGE",FACE,{"derivedFrom":[makeQuery(id+"F9.boolean.opBoolean","COPY",FACE,{"derivedFrom":makeQuery(id+"F9.opExtrude","SWEPT_FACE",FACE,{"disambiguationData":[OSD([subQ0])]})}),makeQuery(id+"F44.opExtrude","SWEPT_FACE",FACE,{"disambiguationData":[OSD([sQuery(id+"F5.wireOp",EDGE,"E10.0"),sQuery(id+"F5.wireOp",EDGE,"E10.1"),sQuery(id+"F5.wireOp",EDGE,"E10.2"),sQuery(id+"F5.wireOp",EDGE,"E10.3"),sQuery(id+"F5.wireOp",EDGE,"E10.4"),sQuery(id+"F5.wireOp",EDGE,"E10.5"),sQuery(id+"F5.wireOp",EDGE,"E10.6"),sQuery(id+"F5.wireOp",EDGE,"E10.7"),subQ0])]})]});}
            var sketch = newSketch(context, id + "F45", { "sketchPlane" : qUnion([Q0])});
            skLineSegment(sketch, "E33.bottom", {"start": v(-7.62, -42.8) * mm, "end": v(7.62, -42.8) * mm});
            skLineSegment(sketch, "E33.top", {"start": v(-7.62, -40.26) * mm, "end": v(7.62, -40.26) * mm});
            skLineSegment(sketch, "E33.left", {"start": v(-7.62, -42.8) * mm, "end": v(-7.62, -40.26) * mm});
            skLineSegment(sketch, "E33.right", {"start": v(7.62, -42.8) * mm, "end": v(7.62, -40.26) * mm});
            skSolve(sketch);
        }
        {
            var Q0;
            Q0=makeQuery(id+"F45.imprint","IMPRINT",FACE,{"disambiguationData":[TD([[makeQuery(id+"F45.imprint","IMPRINT",EDGE,{"derivedFrom":sQuery(id+"F45.wireOp",EDGE,"E33.bottom")}),-1.0]])]});
            extrude(context, id + "F46", {"entities" : qUnion([Q0]), "operationType" : NewBodyOperationType.REMOVE, "oppositeDirection" : true, "depth" : 25.4 * mm});
        }
        {
            var Q0;
            {var subQ0=sQuery(id+"F5.wireOp",EDGE,"E10.7");var subQ1=sQuery(id+"F5.wireOp",EDGE,"E10.6");var subQ2=sQuery(id+"F5.wireOp",EDGE,"E10.5");var subQ3=sQuery(id+"F5.wireOp",EDGE,"E10.4");var subQ4=sQuery(id+"F5.wireOp",EDGE,"E10.3");var subQ5=sQuery(id+"F5.wireOp",EDGE,"E10.2");var subQ6=sQuery(id+"F5.wireOp",EDGE,"E10.1");var subQ7=sQuery(id+"F5.wireOp",EDGE,"E10.0");Q0=makeQuery(id+"F44.boolean.opBoolean","MERGE",FACE,{"derivedFrom":[makeQuery(id+"F6.boolean.opBoolean","COPY",FACE,{"derivedFrom":makeQuery(id+"F6.opExtrude","CAP_FACE",FACE,{"disambiguationData":[OSD([subQ7,subQ6,subQ5,subQ4,subQ3,subQ2,subQ1,subQ0])],"isStart":false})}),makeQuery(id+"F44.opExtrude","CAP_FACE",FACE,{"disambiguationData":[OSD([subQ7,subQ6,subQ5,subQ4,subQ3,subQ2,subQ1,subQ0,sQuery(id+"F8.wireOp",EDGE,"E11.3"),sQuery(id+"F10.wireOp",EDGE,"E12.4"),sQuery(id+"F43.wireOp",EDGE,"E29"),sQuery(id+"F43.wireOp",EDGE,"E30"),sQuery(id+"F43.wireOp",EDGE,"E31"),sQuery(id+"F43.wireOp",EDGE,"E32")])],"isStart":true})]});}
            var sketch = newSketch(context, id + "F47", { "sketchPlane" : qUnion([Q0])});
            skLineSegment(sketch, "E34.bottom", {"start": v(-56.33, 23.24) * mm, "end": v(9.7, 23.24) * mm});
            skLineSegment(sketch, "E34.top", {"start": v(-56.33, 25.78) * mm, "end": v(9.7, 25.78) * mm});
            skLineSegment(sketch, "E34.left", {"start": v(-56.33, 23.24) * mm, "end": v(-56.33, 25.78) * mm});
            skLineSegment(sketch, "E34.right", {"start": v(9.7, 23.24) * mm, "end": v(9.7, 25.78) * mm});
            skSolve(sketch);
        }
        {
            var Q0;
            Q0=makeQuery(id+"F47.imprint","IMPRINT",FACE,{"disambiguationData":[TD([[makeQuery(id+"F47.imprint","IMPRINT",EDGE,{"derivedFrom":sQuery(id+"F47.wireOp",EDGE,"E34.bottom")}),-1.0]])]});
            extrude(context, id + "F48", {"entities" : qUnion([Q0]), "operationType" : NewBodyOperationType.ADD, "oppositeDirection" : true, "depth" : 15.24 * mm});
        }
        {
            var Q0;
            {var subQ0=sQuery(id+"F5.wireOp",EDGE,"E10.7");var subQ1=sQuery(id+"F5.wireOp",EDGE,"E10.6");var subQ2=sQuery(id+"F5.wireOp",EDGE,"E10.5");var subQ3=sQuery(id+"F5.wireOp",EDGE,"E10.4");var subQ4=sQuery(id+"F5.wireOp",EDGE,"E10.3");var subQ5=sQuery(id+"F5.wireOp",EDGE,"E10.2");var subQ6=sQuery(id+"F5.wireOp",EDGE,"E10.1");var subQ7=sQuery(id+"F5.wireOp",EDGE,"E10.0");Q0=makeQuery(id+"F48.boolean.opBoolean","MERGE",FACE,{"derivedFrom":[makeQuery(id+"F44.boolean.opBoolean","MERGE",FACE,{"derivedFrom":[makeQuery(id+"F6.boolean.opBoolean","COPY",FACE,{"derivedFrom":makeQuery(id+"F6.opExtrude","CAP_FACE",FACE,{"disambiguationData":[OSD([subQ7,subQ6,subQ5,subQ4,subQ3,subQ2,subQ1,subQ0])],"isStart":false})}),makeQuery(id+"F44.opExtrude","CAP_FACE",FACE,{"disambiguationData":[OSD([subQ7,subQ6,subQ5,subQ4,subQ3,subQ2,subQ1,subQ0,sQuery(id+"F8.wireOp",EDGE,"E11.3"),sQuery(id+"F10.wireOp",EDGE,"E12.4"),sQuery(id+"F43.wireOp",EDGE,"E29"),sQuery(id+"F43.wireOp",EDGE,"E30"),sQuery(id+"F43.wireOp",EDGE,"E31"),sQuery(id+"F43.wireOp",EDGE,"E32")])],"isStart":true})]}),makeQuery(id+"F48.opExtrude","CAP_FACE",FACE,{"disambiguationData":[OSD([sQuery(id+"F47.wireOp",EDGE,"E34.bottom"),sQuery(id+"F47.wireOp",EDGE,"E34.top"),sQuery(id+"F47.wireOp",EDGE,"E34.left"),sQuery(id+"F47.wireOp",EDGE,"E34.right")])],"isStart":true})]});}
            var sketch = newSketch(context, id + "F49", { "sketchPlane" : qUnion([Q0])});
            skLineSegment(sketch, "E35.bottom", {"start": v(-53.8, 20.7) * mm, "end": v(7.17, 20.7) * mm});
            skLineSegment(sketch, "E35.top", {"start": v(-53.8, 23.24) * mm, "end": v(7.17, 23.24) * mm});
            skLineSegment(sketch, "E35.left", {"start": v(-53.8, 20.7) * mm, "end": v(-53.8, 23.24) * mm});
            skLineSegment(sketch, "E35.right", {"start": v(7.17, 20.7) * mm, "end": v(7.17, 23.24) * mm});
            skSolve(sketch);
        }
        {
            var Q0;
            Q0=makeQuery(id+"F49.imprint","IMPRINT",FACE,{"disambiguationData":[TD([[makeQuery(id+"F49.imprint","IMPRINT",EDGE,{"derivedFrom":sQuery(id+"F49.wireOp",EDGE,"E35.bottom")}),-1.0]])]});
            extrude(context, id + "F50", {"entities" : qUnion([Q0]), "operationType" : NewBodyOperationType.REMOVE, "oppositeDirection" : true, "depth" : 25.4 * mm});
        }
        {
            var Q0;
            Q0=makeQuery(id+"F48.opExtrude","SWEPT_FACE",FACE,{"disambiguationData":[OSD([sQuery(id+"F47.wireOp",EDGE,"E34.top")])]});
            var sketch = newSketch(context, id + "F51", { "sketchPlane" : qUnion([Q0])});
            skLineSegment(sketch, "E36.0", {"start": v(-53.8, -5.08) * mm, "end": v(7.17, -5.08) * mm});
            skLineSegment(sketch, "E36.1", {"start": v(-53.8, 5.08) * mm, "end": v(-53.8, -5.08) * mm});
            skLineSegment(sketch, "E36.2", {"start": v(7.17, 5.08) * mm, "end": v(-53.8, 5.08) * mm});
            skLineSegment(sketch, "E36.3", {"start": v(7.17, -5.08) * mm, "end": v(7.17, 5.08) * mm});
            skSolve(sketch);
        }
        {
            var Q0;
            Q0=makeQuery(id+"F51.imprint","IMPRINT",FACE,{"disambiguationData":[TD([[makeQuery(id+"F51.imprint","IMPRINT",EDGE,{"derivedFrom":sQuery(id+"F51.wireOp",EDGE,"E36.0")}),1.0]])]});
            extrude(context, id + "F52", {"entities" : qUnion([Q0]), "operationType" : NewBodyOperationType.REMOVE, "oppositeDirection" : true, "depth" : 2.54 * mm});
        }
        {
            var Q0;
            Q0=makeQuery(id+"F46.boolean.opBoolean","MERGE",FACE,{"derivedFrom":[makeQuery(id+"F44.opExtrude","SWEPT_FACE",FACE,{"disambiguationData":[OSD([sQuery(id+"F5.wireOp",EDGE,"E10.0"),sQuery(id+"F5.wireOp",EDGE,"E10.1"),sQuery(id+"F5.wireOp",EDGE,"E10.2"),sQuery(id+"F5.wireOp",EDGE,"E10.3"),sQuery(id+"F5.wireOp",EDGE,"E10.4"),sQuery(id+"F5.wireOp",EDGE,"E10.5"),sQuery(id+"F5.wireOp",EDGE,"E10.6"),sQuery(id+"F5.wireOp",EDGE,"E10.7"),sQuery(id+"F10.wireOp",EDGE,"E12.4"),sQuery(id+"F43.wireOp",EDGE,"E29"),sQuery(id+"F43.wireOp",EDGE,"E30")])]}),makeQuery(id+"F46.opExtrude","SWEPT_FACE",FACE,{"disambiguationData":[OSD([sQuery(id+"F45.wireOp",EDGE,"E33.top")])]})]});
            var sketch = newSketch(context, id + "F53", { "sketchPlane" : qUnion([Q0])});
            skLineSegment(sketch, "E37.0", {"start": v(-18.23, 5.08) * mm, "end": v(-28.4, 5.08) * mm});
            skLineSegment(sketch, "E37.1", {"start": v(-18.23, -5.08) * mm, "end": v(-18.23, 5.08) * mm});
            skLineSegment(sketch, "E37.2", {"start": v(-28.4, -5.08) * mm, "end": v(-18.23, -5.08) * mm});
            skLineSegment(sketch, "E37.3", {"start": v(-28.4, 5.08) * mm, "end": v(-28.4, -5.08) * mm});
            skSolve(sketch);
        }
        {
            var Q0;
            Q0=makeQuery(id+"F53.imprint","IMPRINT",FACE,{"disambiguationData":[TD([[makeQuery(id+"F53.imprint","IMPRINT",EDGE,{"derivedFrom":sQuery(id+"F53.wireOp",EDGE,"E37.0")}),1.0]])]});
            extrude(context, id + "F54", {"entities" : qUnion([Q0]), "operationType" : NewBodyOperationType.REMOVE, "oppositeDirection" : true, "depth" : 2.54 * mm});
        }
    });
